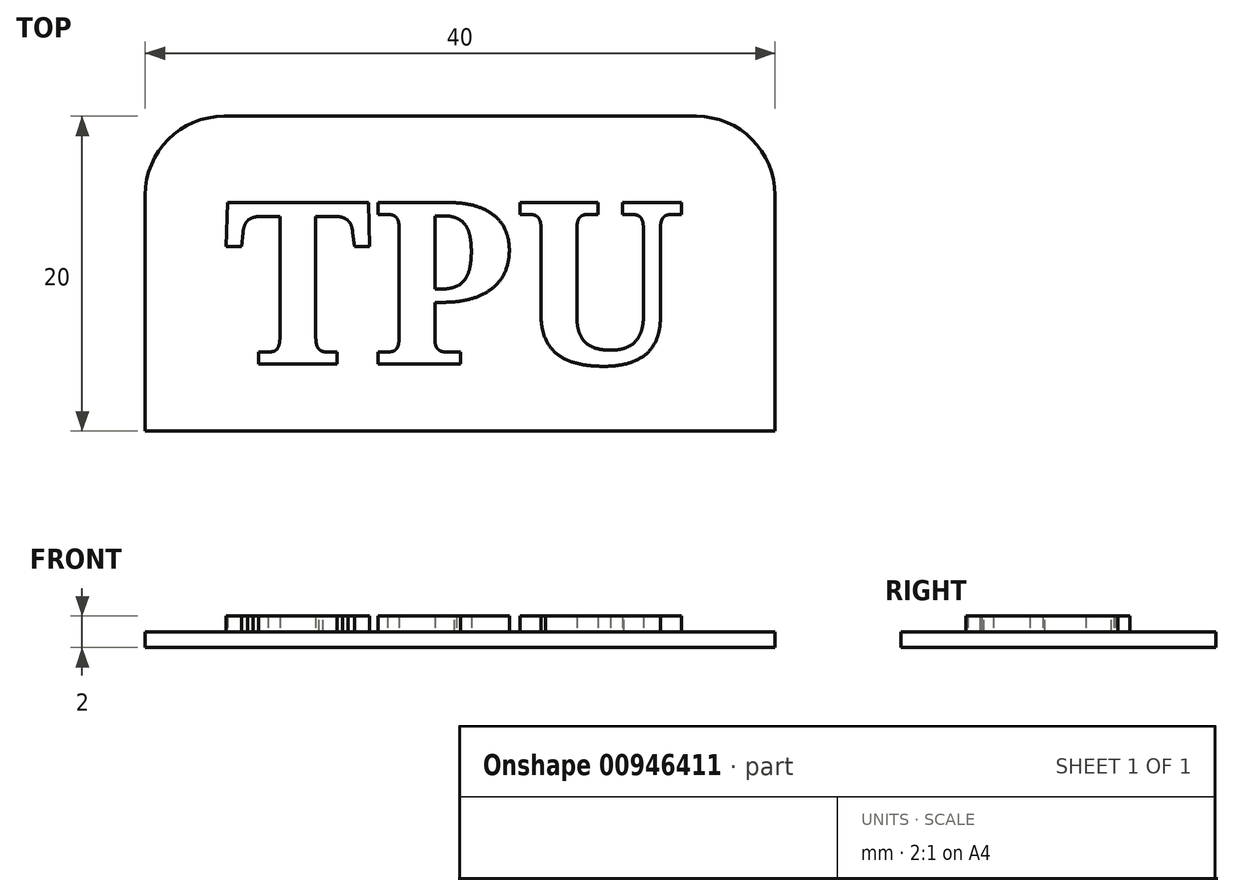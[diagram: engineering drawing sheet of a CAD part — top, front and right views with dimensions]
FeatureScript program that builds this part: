
annotation { "Feature Type Name" : "Feature", "Feature Type Description" : "" }
export const myFeature = defineFeature(function(context is Context, id is Id, definition is map)
    precondition{}
    {
        {
            var Q0;
            Q0=qCreatedBy(makeId("Top.planeOp"),FACE);
            var sketch = newSketch(context, id + "F0", { "sketchPlane" : qUnion([Q0])});
            skLineSegment(sketch, "E0.bottom", {"start": v(-20, 10) * mm, "end": v(20, 10) * mm});
            skLineSegment(sketch, "E0.top", {"start": v(-20, -10) * mm, "end": v(20, -10) * mm});
            skLineSegment(sketch, "E0.left", {"start": v(-20, 10) * mm, "end": v(-20, -10) * mm});
            skLineSegment(sketch, "E0.right", {"start": v(20, 10) * mm, "end": v(20, -10) * mm});
            skPoint(sketch, "E0.middle", {"position": v(0, 0) * mm});
            skSolve(sketch);
        }
        {
            var Q0;
            Q0=makeQuery(id+"F0.imprint","IMPRINT",FACE,{"disambiguationData":[TD([[makeQuery(id+"F0.imprint","IMPRINT",EDGE,{"derivedFrom":sQuery(id+"F0.wireOp",EDGE,"E0.bottom")}),-1.0]])]});
            extrude(context, id + "F1", {"entities" : qUnion([Q0]), "depth" : 1 * mm, "offsetDistance" : 25 * mm});
        }
        {
            var Q0;
            Q0=makeQuery(id+"F1.opExtrude","CAP_FACE",FACE,{"disambiguationData":[OSD([sQuery(id+"F0.wireOp",EDGE,"E0.bottom"),sQuery(id+"F0.wireOp",EDGE,"E0.top"),sQuery(id+"F0.wireOp",EDGE,"E0.left"),sQuery(id+"F0.wireOp",EDGE,"E0.right")])],"isStart":false});
            var sketch = newSketch(context, id + "F2", { "sketchPlane" : qUnion([Q0])});
            skText(sketch, "E1", { "text": "TPU", "fontName": "NotoSerif-Bold.ttf"});
            const initialGuessF2  = {"E1": [-0.015, -0.00574, 1, 0, 0.01035]};
            skSetInitialGuess(sketch, initialGuessF2);
            skSolve(sketch);
        }
        {
            var Q0;
            Q0=qSketchRegion(id+"F2",true);
            extrude(context, id + "F3", {"entities" : qUnion([Q0]), "operationType" : NewBodyOperationType.ADD, "depth" : 1 * mm, "offsetDistance" : 25 * mm});
        }
        {
            var Q0;
            Q0=makeQuery(id+"F1.opExtrude","SWEPT_EDGE",EDGE,{"disambiguationData":[OSD([sQuery(id+"F0.wireOp",EDGE,"E0.bottom"),sQuery(id+"F0.wireOp",EDGE,"E0.left")])]});
            var Q1;
            Q1=makeQuery(id+"F1.opExtrude","SWEPT_EDGE",EDGE,{"disambiguationData":[OSD([sQuery(id+"F0.wireOp",EDGE,"E0.bottom"),sQuery(id+"F0.wireOp",EDGE,"E0.right")])]});
            fillet(context, id + "F4", {"entities" : qUnion([Q0, Q1]), "radius" : 5 * mm, "tangentPropagation" : true, "allowEdgeOverflow" : false});
        }
    });
